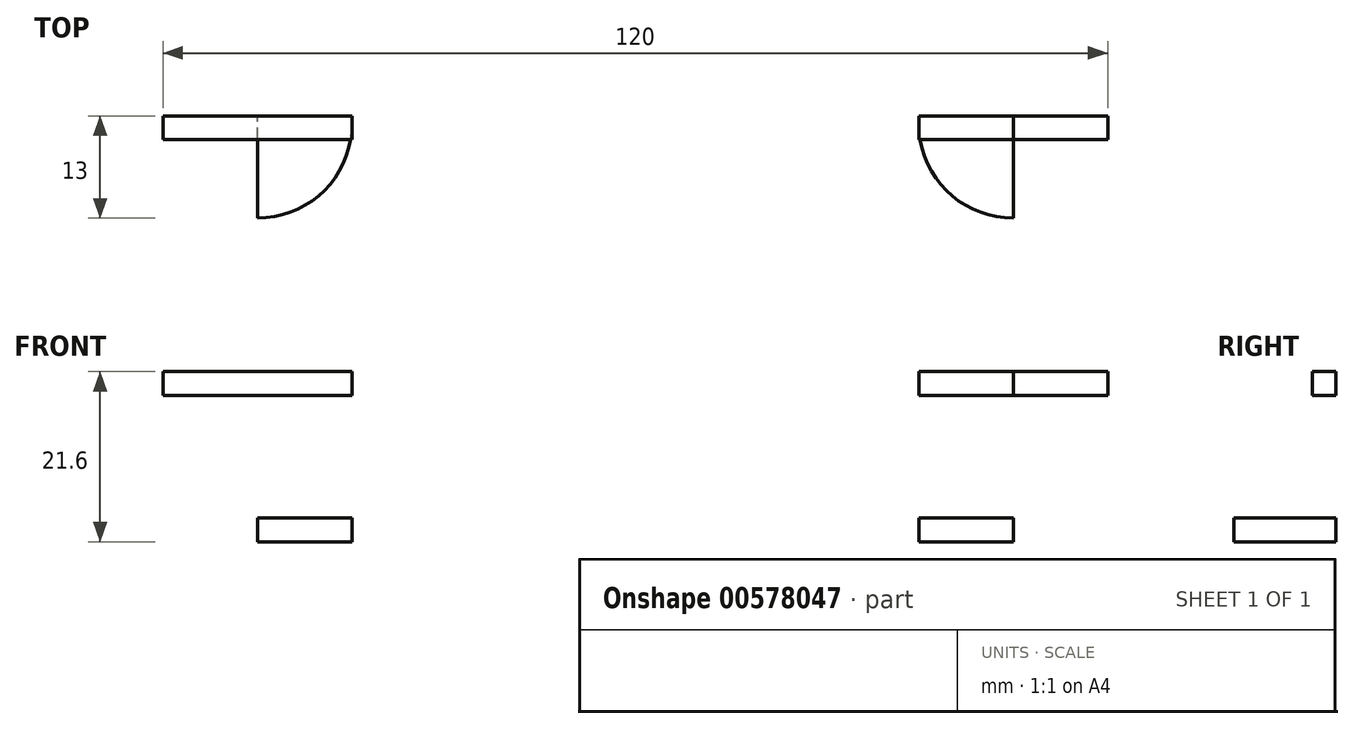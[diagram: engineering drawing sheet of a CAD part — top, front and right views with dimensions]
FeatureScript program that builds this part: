
annotation { "Feature Type Name" : "Feature", "Feature Type Description" : "" }
export const myFeature = defineFeature(function(context is Context, id is Id, definition is map)
    precondition{}
    {
        {
            var Q0;
            Q0=qCreatedBy(makeId("Front.planeOp"),FACE);
            var sketch = newSketch(context, id + "F0", { "sketchPlane" : qUnion([Q0])});
            skLineSegment(sketch, "E0.bottom", {"start": v(-60, 10.8) * mm, "end": v(60, 10.8) * mm});
            skLineSegment(sketch, "E0.top", {"start": v(-60, -10.8) * mm, "end": v(60, -10.8) * mm});
            skLineSegment(sketch, "E0.left", {"start": v(-60, 10.8) * mm, "end": v(-60, -10.8) * mm});
            skLineSegment(sketch, "E0.right", {"start": v(60, 10.8) * mm, "end": v(60, -10.8) * mm});
            skPoint(sketch, "E0.middle", {"position": v(0, 0) * mm});
            skLineSegment(sketch, "E1.bottom", {"start": v(-60, 10.8) * mm, "end": v(-48, 10.8) * mm});
            skLineSegment(sketch, "E1.top", {"start": v(-60, 7.8) * mm, "end": v(-48, 7.8) * mm});
            skLineSegment(sketch, "E1.left", {"start": v(-60, 10.8) * mm, "end": v(-60, 7.8) * mm});
            skLineSegment(sketch, "E1.right", {"start": v(-48, 10.8) * mm, "end": v(-48, 7.8) * mm});
            skLineSegment(sketch, "E2.bottom", {"start": v(60, 10.8) * mm, "end": v(48, 10.8) * mm});
            skLineSegment(sketch, "E2.top", {"start": v(60, 7.8) * mm, "end": v(48, 7.8) * mm});
            skLineSegment(sketch, "E2.left", {"start": v(60, 10.8) * mm, "end": v(60, 7.8) * mm});
            skLineSegment(sketch, "E2.right", {"start": v(48, 10.8) * mm, "end": v(48, 7.8) * mm});
            skLineSegment(sketch, "E3.bottom", {"start": v(-60, -10.8) * mm, "end": v(-48, -10.8) * mm});
            skLineSegment(sketch, "E3.top", {"start": v(-60, -7.8) * mm, "end": v(-48, -7.8) * mm});
            skLineSegment(sketch, "E3.left", {"start": v(-60, -10.8) * mm, "end": v(-60, -7.8) * mm});
            skLineSegment(sketch, "E3.right", {"start": v(-48, -10.8) * mm, "end": v(-48, -7.8) * mm});
            skLineSegment(sketch, "E4.bottom", {"start": v(60, -10.8) * mm, "end": v(48, -10.8) * mm});
            skLineSegment(sketch, "E4.top", {"start": v(60, -7.8) * mm, "end": v(48, -7.8) * mm});
            skLineSegment(sketch, "E4.left", {"start": v(60, -10.8) * mm, "end": v(60, -7.8) * mm});
            skLineSegment(sketch, "E4.right", {"start": v(48, -10.8) * mm, "end": v(48, -7.8) * mm});
            skLineSegment(sketch, "E5.bottom", {"start": v(-48, 10.8) * mm, "end": v(-36, 10.8) * mm});
            skLineSegment(sketch, "E5.top", {"start": v(-48, 7.8) * mm, "end": v(-36, 7.8) * mm});
            skLineSegment(sketch, "E5.right", {"start": v(-36, 10.8) * mm, "end": v(-36, 7.8) * mm});
            skLineSegment(sketch, "E6.bottom", {"start": v(48, 7.8) * mm, "end": v(36, 7.8) * mm});
            skLineSegment(sketch, "E6.top", {"start": v(48, 10.8) * mm, "end": v(36, 10.8) * mm});
            skLineSegment(sketch, "E6.left", {"start": v(48, 7.8) * mm, "end": v(48, 10.8) * mm});
            skLineSegment(sketch, "E6.right", {"start": v(36, 7.8) * mm, "end": v(36, 10.8) * mm});
            skLineSegment(sketch, "E7.bottom", {"start": v(-48, -7.8) * mm, "end": v(-36, -7.8) * mm});
            skLineSegment(sketch, "E7.top", {"start": v(-48, -10.8) * mm, "end": v(-36, -10.8) * mm});
            skLineSegment(sketch, "E7.left", {"start": v(-48, -7.8) * mm, "end": v(-48, -10.8) * mm});
            skLineSegment(sketch, "E7.right", {"start": v(-36, -7.8) * mm, "end": v(-36, -10.8) * mm});
            skLineSegment(sketch, "E8.bottom", {"start": v(48, -7.8) * mm, "end": v(36, -7.8) * mm});
            skLineSegment(sketch, "E8.top", {"start": v(48, -10.8) * mm, "end": v(36, -10.8) * mm});
            skLineSegment(sketch, "E8.left", {"start": v(48, -7.8) * mm, "end": v(48, -10.8) * mm});
            skLineSegment(sketch, "E8.right", {"start": v(36, -7.8) * mm, "end": v(36, -10.8) * mm});
            skSolve(sketch);
        }
        {
            var Q0;
            Q0=makeQuery(id+"F0.imprint","IMPRINT",FACE,{"disambiguationData":[TD([[makeQuery(id+"F0.imprint","IMPRINT",EDGE,{"derivedFrom":sQuery(id+"F0.wireOp",EDGE,"E0.bottom")}),-1.0]])]});
            extrude(context, id + "F1", {"entities" : qUnion([Q0]), "depth" : 3 * mm, "offsetDistance" : 25 * mm});
        }
        {
            var Q0;
            Q0=makeQuery(id+"F0.imprint","IMPRINT",FACE,{"disambiguationData":[TD([[makeQuery(id+"F0.imprint","IMPRINT",EDGE,{"derivedFrom":sQuery(id+"F0.wireOp",EDGE,"E3.bottom")}),1.0]])]});
            var Q1;
            Q1=makeQuery(id+"F0.imprint","IMPRINT",FACE,{"disambiguationData":[TD([[makeQuery(id+"F0.imprint","IMPRINT",EDGE,{"derivedFrom":sQuery(id+"F0.wireOp",EDGE,"E4.bottom")}),-1.0]])]});
            var Q2;
            Q2=makeQuery(id+"F0.imprint","IMPRINT",FACE,{"disambiguationData":[TD([[makeQuery(id+"F0.imprint","IMPRINT",EDGE,{"derivedFrom":sQuery(id+"F0.wireOp",EDGE,"E7.bottom")}),-1.0]])]});
            var Q3;
            Q3=makeQuery(id+"F0.imprint","IMPRINT",FACE,{"disambiguationData":[TD([[makeQuery(id+"F0.imprint","IMPRINT",EDGE,{"derivedFrom":sQuery(id+"F0.wireOp",EDGE,"E8.bottom")}),1.0]])]});
            extrude(context, id + "F2", {"entities" : qUnion([Q0, Q1, Q2, Q3]), "operationType" : NewBodyOperationType.ADD, "depth" : 13 * mm, "offsetDistance" : 25 * mm});
        }
        {
            var Q0;
            Q0=makeQuery(id+"F2.opExtrude","CAP_EDGE",EDGE,{"disambiguationData":[OSD([sQuery(id+"F0.wireOp",EDGE,"E7.right")])],"isStart":false});
            fillet(context, id + "F3", {"entities" : qUnion([Q0]), "radius" : 12 * mm, "tangentPropagation" : true, "allowEdgeOverflow" : false});
        }
        {
            var Q0;
            Q0=makeQuery(id+"F2.opExtrude","CAP_EDGE",EDGE,{"disambiguationData":[OSD([sQuery(id+"F0.wireOp",EDGE,"E8.right")])],"isStart":false});
            fillet(context, id + "F4", {"entities" : qUnion([Q0]), "radius" : 12 * mm, "tangentPropagation" : true, "allowEdgeOverflow" : false});
        }
        {
            var Q0;
            Q0=makeQuery(id+"F0.imprint","IMPRINT",FACE,{"disambiguationData":[TD([[makeQuery(id+"F0.imprint","IMPRINT",EDGE,{"derivedFrom":sQuery(id+"F0.wireOp",EDGE,"E1.bottom")}),-1.0]])]});
            var Q1;
            Q1=makeQuery(id+"F0.imprint","IMPRINT",FACE,{"disambiguationData":[TD([[makeQuery(id+"F0.imprint","IMPRINT",EDGE,{"derivedFrom":sQuery(id+"F0.wireOp",EDGE,"E5.bottom")}),-1.0]])]});
            var Q2;
            Q2=makeQuery(id+"F0.imprint","IMPRINT",FACE,{"disambiguationData":[TD([[makeQuery(id+"F0.imprint","IMPRINT",EDGE,{"derivedFrom":sQuery(id+"F0.wireOp",EDGE,"E6.bottom")}),-1.0]])]});
            var Q3;
            Q3=makeQuery(id+"F0.imprint","IMPRINT",FACE,{"disambiguationData":[TD([[makeQuery(id+"F0.imprint","IMPRINT",EDGE,{"derivedFrom":sQuery(id+"F0.wireOp",EDGE,"E2.bottom")}),1.0]])]});
            extrude(context, id + "F5", {"entities" : qUnion([Q0, Q1, Q2, Q3]), "oppositeDirection" : true, "depth" : 15 * mm, "offsetDistance" : 25 * mm});
        }
        {
            var Q0;
            Q0=makeQuery(id+"F5.opExtrude","SWEPT_BODY",BODY,{"disambiguationData":[OSD([sQuery(id+"F0.wireOp",EDGE,"E1.bottom"),sQuery(id+"F0.wireOp",EDGE,"E1.top"),sQuery(id+"F0.wireOp",EDGE,"E1.left"),sQuery(id+"F0.wireOp",EDGE,"E5.bottom"),sQuery(id+"F0.wireOp",EDGE,"E5.top"),sQuery(id+"F0.wireOp",EDGE,"E5.right")])]});
            var Q1;
            Q1=makeQuery(id+"F5.opExtrude","SWEPT_BODY",BODY,{"disambiguationData":[OSD([sQuery(id+"F0.wireOp",EDGE,"E2.bottom"),sQuery(id+"F0.wireOp",EDGE,"E2.top"),sQuery(id+"F0.wireOp",EDGE,"E2.left"),sQuery(id+"F0.wireOp",EDGE,"E6.bottom"),sQuery(id+"F0.wireOp",EDGE,"E6.top"),sQuery(id+"F0.wireOp",EDGE,"E6.right")])]});
            transform(context, id + "F6", {"entities" : qUnion([Q0, Q1]), "transformType" : TransformType.TRANSLATION_3D, "dx" : 0 * mm, "dy" : -3 * mm, "dz" : 0 * mm, "makeCopy" : false});
        }
        {
            var Q0;
            Q0=makeQuery(id+"F5.opExtrude","CAP_EDGE",EDGE,{"disambiguationData":[OSD([sQuery(id+"F0.wireOp",EDGE,"E5.right")])],"isStart":false});
            var Q1;
            Q1=makeQuery(id+"F5.opExtrude","CAP_EDGE",EDGE,{"disambiguationData":[OSD([sQuery(id+"F0.wireOp",EDGE,"E6.right")])],"isStart":false});
            fillet(context, id + "F7", {"entities" : qUnion([Q0, Q1]), "radius" : 12 * mm, "tangentPropagation" : true, "allowEdgeOverflow" : false});
        }
        {
            var Q0;
            Q0=qCreatedBy(makeId("Top.planeOp"),FACE);
            var sketch = newSketch(context, id + "F8", { "sketchPlane" : qUnion([Q0])});
            skLineSegment(sketch, "E9.bottom", {"start": v(-60, 0) * mm, "end": v(60, 0) * mm});
            skLineSegment(sketch, "E9.top", {"start": v(-60, 12) * mm, "end": v(60, 12) * mm});
            skLineSegment(sketch, "E9.left", {"start": v(-60, 0) * mm, "end": v(-60, 12) * mm});
            skLineSegment(sketch, "E9.right", {"start": v(60, 0) * mm, "end": v(60, 12) * mm});
            skLineSegment(sketch, "E10.0", {"start": v(-60, 7) * mm, "end": v(60, 7) * mm});
            skLineSegment(sketch, "E11.0", {"start": v(-53, 0) * mm, "end": v(-53, 12) * mm});
            skLineSegment(sketch, "E12.0", {"start": v(53, 0) * mm, "end": v(53, 12) * mm});
            skCircle(sketch, "E13", {"center": v(-53, 7) * mm, "radius": 1.75 * mm});
            skCircle(sketch, "E14", {"center": v(53, 7) * mm, "radius": 1.75 * mm});
            skLineSegment(sketch, "E15.bottom", {"start": v(-60.02, -3.21) * mm, "end": v(59.98, -3.21) * mm});
            skLineSegment(sketch, "E15.top", {"start": v(-60.02, -13.21) * mm, "end": v(59.98, -13.21) * mm});
            skLineSegment(sketch, "E15.left", {"start": v(-60.02, -3.21) * mm, "end": v(-60.02, -13.21) * mm});
            skLineSegment(sketch, "E15.right", {"start": v(59.98, -3.21) * mm, "end": v(59.98, -13.21) * mm});
            skLineSegment(sketch, "E16.0", {"start": v(-60.02, -8.21) * mm, "end": v(59.98, -8.21) * mm});
            skLineSegment(sketch, "E17.0", {"start": v(-48.02, -3.21) * mm, "end": v(-48.02, -13.21) * mm});
            skLineSegment(sketch, "E18.0", {"start": v(47.98, -3.21) * mm, "end": v(47.98, -13.21) * mm});
            skCircle(sketch, "E19", {"center": v(-48.02, -8.21) * mm, "radius": 1.75 * mm});
            skCircle(sketch, "E20", {"center": v(47.98, -8.21) * mm, "radius": 1.75 * mm});
            skSolve(sketch);
        }
        {
            var Q0;
            {var subQ0=sQuery(id+"F8.wireOp",EDGE,"E13");var subQ1=sQuery(id+"F8.wireOp",EDGE,"E10.0");var subQ2=makeQuery(id+"F8.imprint","INTERSECT",VERTEX,{"disambiguationData":[OD(0.0)],"derivedFrom":[subQ1,subQ0]});Q0=makeQuery(id+"F8.imprint","IMPRINT",FACE,{"disambiguationData":[TD([[makeQuery(id+"F8.imprint","IMPRINT",EDGE,{"disambiguationData":[TD([[subQ2,-1.0]])],"derivedFrom":subQ1}),1.0]])]});}
            var Q1;
            {var subQ0=sQuery(id+"F8.wireOp",EDGE,"E11.0");var subQ1=sQuery(id+"F8.wireOp",EDGE,"E10.0");var subQ2=makeQuery(id+"F8.imprint","INTERSECT",VERTEX,{"derivedFrom":[subQ1,subQ0]});Q1=makeQuery(id+"F8.imprint","IMPRINT",FACE,{"disambiguationData":[TD([[makeQuery(id+"F8.imprint","IMPRINT",EDGE,{"disambiguationData":[TD([[subQ2,-1.0]])],"derivedFrom":subQ1}),1.0]])]});}
            var Q2;
            {var subQ0=sQuery(id+"F8.wireOp",EDGE,"E11.0");var subQ1=sQuery(id+"F8.wireOp",EDGE,"E10.0");var subQ2=makeQuery(id+"F8.imprint","INTERSECT",VERTEX,{"derivedFrom":[subQ1,subQ0]});Q2=makeQuery(id+"F8.imprint","IMPRINT",FACE,{"disambiguationData":[TD([[makeQuery(id+"F8.imprint","IMPRINT",EDGE,{"disambiguationData":[TD([[subQ2,-1.0]])],"derivedFrom":subQ1}),-1.0]])]});}
            var Q3;
            {var subQ0=sQuery(id+"F8.wireOp",EDGE,"E13");var subQ1=sQuery(id+"F8.wireOp",EDGE,"E10.0");var subQ2=makeQuery(id+"F8.imprint","INTERSECT",VERTEX,{"disambiguationData":[OD(0.0)],"derivedFrom":[subQ1,subQ0]});Q3=makeQuery(id+"F8.imprint","IMPRINT",FACE,{"disambiguationData":[TD([[makeQuery(id+"F8.imprint","IMPRINT",EDGE,{"disambiguationData":[TD([[subQ2,-1.0]])],"derivedFrom":subQ1}),-1.0]])]});}
            var Q4;
            {var subQ0=sQuery(id+"F8.wireOp",EDGE,"E14");var subQ1=sQuery(id+"F8.wireOp",EDGE,"E10.0");var subQ2=makeQuery(id+"F8.imprint","INTERSECT",VERTEX,{"disambiguationData":[OD(0.0)],"derivedFrom":[subQ1,subQ0]});Q4=makeQuery(id+"F8.imprint","IMPRINT",FACE,{"disambiguationData":[TD([[makeQuery(id+"F8.imprint","IMPRINT",EDGE,{"disambiguationData":[TD([[subQ2,-1.0]])],"derivedFrom":subQ1}),-1.0]])]});}
            var Q5;
            {var subQ0=sQuery(id+"F8.wireOp",EDGE,"E12.0");var subQ1=sQuery(id+"F8.wireOp",EDGE,"E10.0");var subQ2=makeQuery(id+"F8.imprint","INTERSECT",VERTEX,{"derivedFrom":[subQ1,subQ0]});Q5=makeQuery(id+"F8.imprint","IMPRINT",FACE,{"disambiguationData":[TD([[makeQuery(id+"F8.imprint","IMPRINT",EDGE,{"disambiguationData":[TD([[subQ2,-1.0]])],"derivedFrom":subQ1}),-1.0]])]});}
            var Q6;
            {var subQ0=sQuery(id+"F8.wireOp",EDGE,"E12.0");var subQ1=sQuery(id+"F8.wireOp",EDGE,"E10.0");var subQ2=makeQuery(id+"F8.imprint","INTERSECT",VERTEX,{"derivedFrom":[subQ1,subQ0]});Q6=makeQuery(id+"F8.imprint","IMPRINT",FACE,{"disambiguationData":[TD([[makeQuery(id+"F8.imprint","IMPRINT",EDGE,{"disambiguationData":[TD([[subQ2,-1.0]])],"derivedFrom":subQ1}),1.0]])]});}
            var Q7;
            {var subQ0=sQuery(id+"F8.wireOp",EDGE,"E14");var subQ1=sQuery(id+"F8.wireOp",EDGE,"E10.0");var subQ2=makeQuery(id+"F8.imprint","INTERSECT",VERTEX,{"disambiguationData":[OD(0.0)],"derivedFrom":[subQ1,subQ0]});Q7=makeQuery(id+"F8.imprint","IMPRINT",FACE,{"disambiguationData":[TD([[makeQuery(id+"F8.imprint","IMPRINT",EDGE,{"disambiguationData":[TD([[subQ2,-1.0]])],"derivedFrom":subQ1}),1.0]])]});}
            extrude(context, id + "F9", {"entities" : qUnion([Q0, Q1, Q2, Q3, Q4, Q5, Q6, Q7]), "depth" : 25 * mm, "offsetDistance" : 25 * mm});
        }
        {
            var Q0;
            Q0=makeQuery(id+"F9.opExtrude","SWEPT_BODY",BODY,{"disambiguationData":[OSD([sQuery(id+"F8.wireOp",EDGE,"E13")])]});
            var Q1;
            Q1=makeQuery(id+"F9.opExtrude","SWEPT_BODY",BODY,{"disambiguationData":[OSD([sQuery(id+"F8.wireOp",EDGE,"E14")])]});
            var Q2;
            Q2=makeQuery(id+"F5.opExtrude","SWEPT_BODY",BODY,{"disambiguationData":[OSD([sQuery(id+"F0.wireOp",EDGE,"E1.bottom"),sQuery(id+"F0.wireOp",EDGE,"E1.top"),sQuery(id+"F0.wireOp",EDGE,"E1.left"),sQuery(id+"F0.wireOp",EDGE,"E5.bottom"),sQuery(id+"F0.wireOp",EDGE,"E5.top"),sQuery(id+"F0.wireOp",EDGE,"E5.right")])]});
            var Q3;
            Q3=makeQuery(id+"F5.opExtrude","SWEPT_BODY",BODY,{"disambiguationData":[OSD([sQuery(id+"F0.wireOp",EDGE,"E2.bottom"),sQuery(id+"F0.wireOp",EDGE,"E2.top"),sQuery(id+"F0.wireOp",EDGE,"E2.left"),sQuery(id+"F0.wireOp",EDGE,"E6.bottom"),sQuery(id+"F0.wireOp",EDGE,"E6.top"),sQuery(id+"F0.wireOp",EDGE,"E6.right")])]});
            booleanBodies(context, id + "F10", {"operationType" : BooleanOperationType.SUBTRACTION, "tools" : qUnion([Q0, Q1]), "targets" : qUnion([Q2, Q3])});
        }
        {
            var Q0;
            {var subQ0=sQuery(id+"F8.wireOp",EDGE,"E17.0");var subQ1=sQuery(id+"F8.wireOp",EDGE,"E16.0");var subQ2=makeQuery(id+"F8.imprint","INTERSECT",VERTEX,{"derivedFrom":[subQ1,subQ0]});Q0=makeQuery(id+"F8.imprint","IMPRINT",FACE,{"disambiguationData":[TD([[makeQuery(id+"F8.imprint","IMPRINT",EDGE,{"disambiguationData":[TD([[subQ2,-1.0]])],"derivedFrom":subQ1}),1.0]])]});}
            var Q1;
            {var subQ0=sQuery(id+"F8.wireOp",EDGE,"E19");var subQ1=sQuery(id+"F8.wireOp",EDGE,"E16.0");var subQ2=makeQuery(id+"F8.imprint","INTERSECT",VERTEX,{"disambiguationData":[OD(0.0)],"derivedFrom":[subQ1,subQ0]});Q1=makeQuery(id+"F8.imprint","IMPRINT",FACE,{"disambiguationData":[TD([[makeQuery(id+"F8.imprint","IMPRINT",EDGE,{"disambiguationData":[TD([[subQ2,-1.0]])],"derivedFrom":subQ1}),1.0]])]});}
            var Q2;
            {var subQ0=sQuery(id+"F8.wireOp",EDGE,"E19");var subQ1=sQuery(id+"F8.wireOp",EDGE,"E16.0");var subQ2=makeQuery(id+"F8.imprint","INTERSECT",VERTEX,{"disambiguationData":[OD(0.0)],"derivedFrom":[subQ1,subQ0]});Q2=makeQuery(id+"F8.imprint","IMPRINT",FACE,{"disambiguationData":[TD([[makeQuery(id+"F8.imprint","IMPRINT",EDGE,{"disambiguationData":[TD([[subQ2,-1.0]])],"derivedFrom":subQ1}),-1.0]])]});}
            var Q3;
            {var subQ0=sQuery(id+"F8.wireOp",EDGE,"E17.0");var subQ1=sQuery(id+"F8.wireOp",EDGE,"E16.0");var subQ2=makeQuery(id+"F8.imprint","INTERSECT",VERTEX,{"derivedFrom":[subQ1,subQ0]});Q3=makeQuery(id+"F8.imprint","IMPRINT",FACE,{"disambiguationData":[TD([[makeQuery(id+"F8.imprint","IMPRINT",EDGE,{"disambiguationData":[TD([[subQ2,-1.0]])],"derivedFrom":subQ1}),-1.0]])]});}
            var Q4;
            {var subQ0=sQuery(id+"F8.wireOp",EDGE,"E18.0");var subQ1=sQuery(id+"F8.wireOp",EDGE,"E16.0");var subQ2=makeQuery(id+"F8.imprint","INTERSECT",VERTEX,{"derivedFrom":[subQ1,subQ0]});Q4=makeQuery(id+"F8.imprint","IMPRINT",FACE,{"disambiguationData":[TD([[makeQuery(id+"F8.imprint","IMPRINT",EDGE,{"disambiguationData":[TD([[subQ2,-1.0]])],"derivedFrom":subQ1}),1.0]])]});}
            var Q5;
            {var subQ0=sQuery(id+"F8.wireOp",EDGE,"E20");var subQ1=sQuery(id+"F8.wireOp",EDGE,"E16.0");var subQ2=makeQuery(id+"F8.imprint","INTERSECT",VERTEX,{"disambiguationData":[OD(0.0)],"derivedFrom":[subQ1,subQ0]});Q5=makeQuery(id+"F8.imprint","IMPRINT",FACE,{"disambiguationData":[TD([[makeQuery(id+"F8.imprint","IMPRINT",EDGE,{"disambiguationData":[TD([[subQ2,-1.0]])],"derivedFrom":subQ1}),1.0]])]});}
            var Q6;
            {var subQ0=sQuery(id+"F8.wireOp",EDGE,"E20");var subQ1=sQuery(id+"F8.wireOp",EDGE,"E16.0");var subQ2=makeQuery(id+"F8.imprint","INTERSECT",VERTEX,{"disambiguationData":[OD(0.0)],"derivedFrom":[subQ1,subQ0]});Q6=makeQuery(id+"F8.imprint","IMPRINT",FACE,{"disambiguationData":[TD([[makeQuery(id+"F8.imprint","IMPRINT",EDGE,{"disambiguationData":[TD([[subQ2,-1.0]])],"derivedFrom":subQ1}),-1.0]])]});}
            var Q7;
            {var subQ0=sQuery(id+"F8.wireOp",EDGE,"E18.0");var subQ1=sQuery(id+"F8.wireOp",EDGE,"E16.0");var subQ2=makeQuery(id+"F8.imprint","INTERSECT",VERTEX,{"derivedFrom":[subQ1,subQ0]});Q7=makeQuery(id+"F8.imprint","IMPRINT",FACE,{"disambiguationData":[TD([[makeQuery(id+"F8.imprint","IMPRINT",EDGE,{"disambiguationData":[TD([[subQ2,-1.0]])],"derivedFrom":subQ1}),-1.0]])]});}
            extrude(context, id + "F11", {"entities" : qUnion([Q0, Q1, Q2, Q3, Q4, Q5, Q6, Q7]), "oppositeDirection" : true, "depth" : 25 * mm, "offsetDistance" : 25 * mm});
        }
        {
            var Q0;
            Q0=makeQuery(id+"F11.opExtrude","SWEPT_BODY",BODY,{"disambiguationData":[OSD([sQuery(id+"F8.wireOp",EDGE,"E19")])]});
            var Q1;
            Q1=makeQuery(id+"F11.opExtrude","SWEPT_BODY",BODY,{"disambiguationData":[OSD([sQuery(id+"F8.wireOp",EDGE,"E20")])]});
            var Q2;
            Q2=makeQuery(id+"F1.opExtrude","SWEPT_BODY",BODY,{"disambiguationData":[OSD([sQuery(id+"F0.wireOp",EDGE,"E0.bottom"),sQuery(id+"F0.wireOp",EDGE,"E0.top"),sQuery(id+"F0.wireOp",EDGE,"E0.left"),sQuery(id+"F0.wireOp",EDGE,"E0.right"),sQuery(id+"F0.wireOp",EDGE,"E1.top"),sQuery(id+"F0.wireOp",EDGE,"E2.top"),sQuery(id+"F0.wireOp",EDGE,"E3.top"),sQuery(id+"F0.wireOp",EDGE,"E4.top"),sQuery(id+"F0.wireOp",EDGE,"E5.top"),sQuery(id+"F0.wireOp",EDGE,"E5.right"),sQuery(id+"F0.wireOp",EDGE,"E6.bottom"),sQuery(id+"F0.wireOp",EDGE,"E6.right"),sQuery(id+"F0.wireOp",EDGE,"E7.bottom"),sQuery(id+"F0.wireOp",EDGE,"E7.right"),sQuery(id+"F0.wireOp",EDGE,"E8.bottom"),sQuery(id+"F0.wireOp",EDGE,"E8.right")])]});
            booleanBodies(context, id + "F12", {"operationType" : BooleanOperationType.SUBTRACTION, "tools" : qUnion([Q0, Q1]), "targets" : qUnion([Q2])});
        }
    });
